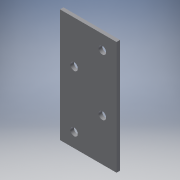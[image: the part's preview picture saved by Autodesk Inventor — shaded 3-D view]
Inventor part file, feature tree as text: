
AUTODESK INVENTOR PART (.ipt)
format: ipt  version: 2016 (Build 200138000, 138)  size: 104,960 bytes
history: native  units: in
note: dims shown in document units (in); Inventor stores cm internally (conversion verified against a paired STEP export)
features: extrude x1, sketch x1
ambient origin geometry x8: Origin, YZ Plane, XZ Plane, XY Plane, X Axis, Y Axis, Z Axis, Center Point
bodies: Solid1 (feature_tree)
feature tree (2):
  extrude  "Extrusion1"  Depth=4.0in
  sketch  "Sketch1"  dims[d0=2.0in d1=4.0in d2=0.2656in d3=0.2656in d4=0.2656in d5=0.2656in d6=0.5in d7=1.5in d8=0.5in d9=0.5in d10=0.5in d11=1.5in d12=0.5in d13=0.5in d14=0.125in d15=0.0in]
